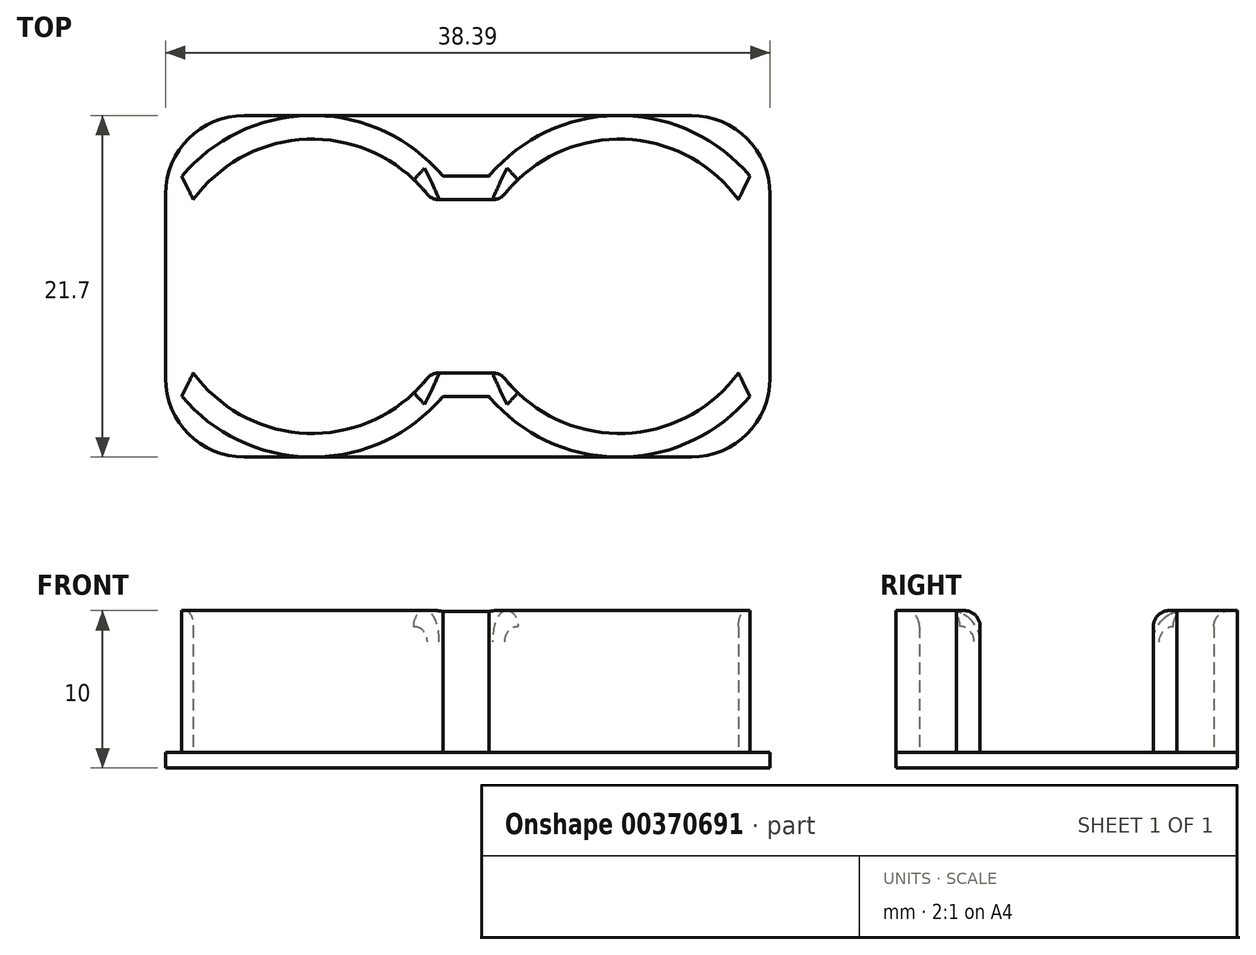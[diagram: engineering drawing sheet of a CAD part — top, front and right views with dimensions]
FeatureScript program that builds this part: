
annotation { "Feature Type Name" : "Feature", "Feature Type Description" : "" }
export const myFeature = defineFeature(function(context is Context, id is Id, definition is map)
    precondition{}
    {
        {
            var Q0;
            Q0=qCreatedBy(makeId("Top.planeOp"),FACE);
            var sketch = newSketch(context, id + "F0", { "sketchPlane" : qUnion([Q0])});
            skArc(sketch, "E0.1.0.0", {"start": v(11.94, -5.5) * mm, "mid": v(19.5, -9.35) * mm, "end": v(27.06, -5.5) * mm});
            skArc(sketch, "E0.2.0.0", {"start": v(31.44, -5.5) * mm, "mid": v(39, -9.35) * mm, "end": v(46.56, -5.5) * mm});
            skLineSegment(sketch, "E0.direction1", {"start": v(0, 0) * mm, "end": v(19.5, 0) * mm, "construction": true});
            skLineSegment(sketch, "E1.trimOffspring", {"start": v(27.06, 5.5) * mm, "end": v(31.44, 5.5) * mm});
            skLineSegment(sketch, "E2.MirrorCS", {"start": v(27.06, -5.5) * mm, "end": v(31.44, -5.5) * mm});
            skArc(sketch, "E3.trimOffspring", {"start": v(27.06, 5.5) * mm, "mid": v(19.5, 9.35) * mm, "end": v(11.94, 5.5) * mm});
            skArc(sketch, "E4.trimOffspring", {"start": v(46.56, 5.5) * mm, "mid": v(39, 9.35) * mm, "end": v(31.44, 5.5) * mm});
            skArc(sketch, "E5.3", {"start": v(47.29, 7) * mm, "mid": v(39, 10.85) * mm, "end": v(30.71, 7) * mm});
            skArc(sketch, "E5.7", {"start": v(30.71, -7) * mm, "mid": v(39, -10.85) * mm, "end": v(47.29, -7) * mm});
            skLineSegment(sketch, "E6.1.0.0", {"start": v(27.79, 7) * mm, "end": v(30.71, 7) * mm});
            skLineSegment(sketch, "E7.MirrorCS", {"start": v(27.79, -7) * mm, "end": v(30.71, -7) * mm});
            skArc(sketch, "E8.trimOffspring", {"start": v(27.79, 7) * mm, "mid": v(19.5, 10.85) * mm, "end": v(11.21, 7) * mm});
            skArc(sketch, "E9.trimOffspring", {"start": v(11.21, -7) * mm, "mid": v(19.5, -10.85) * mm, "end": v(27.79, -7) * mm});
            skLineSegment(sketch, "E10", {"start": v(11.94, 5.5) * mm, "end": v(11.21, 7) * mm});
            skLineSegment(sketch, "E11", {"start": v(46.56, 5.5) * mm, "end": v(47.29, 7) * mm});
            skLineSegment(sketch, "E12", {"start": v(47.29, -7) * mm, "end": v(46.56, -5.5) * mm});
            skLineSegment(sketch, "E13", {"start": v(11.21, -7) * mm, "end": v(11.94, -5.5) * mm});
            skSolve(sketch);
        }
        {
            var Q0;
            Q0=qCreatedBy(makeId("Top.planeOp"),FACE);
            var sketch = newSketch(context, id + "F1", { "sketchPlane" : qUnion([Q0])});
            skArc(sketch, "E14", {"start": v(7.52, 5.55) * mm, "mid": v(-9.35, 0) * mm, "end": v(7.52, -5.55) * mm});
            skArc(sketch, "E15.2.0.0", {"start": v(29.28, -5.55) * mm, "mid": v(36.8, -9.35) * mm, "end": v(44.32, -5.55) * mm});
            skLineSegment(sketch, "E15.direction1", {"start": v(0, 0) * mm, "end": v(18.5, 0) * mm, "construction": true});
            skArc(sketch, "E16.0", {"start": v(8.15, 7.16) * mm, "mid": v(-10.85, 0) * mm, "end": v(8.15, -7.16) * mm});
            skArc(sketch, "E17.0", {"start": v(28.65, -7.16) * mm, "mid": v(36.8, -10.85) * mm, "end": v(44.95, -7.16) * mm});
            skLineSegment(sketch, "E18", {"start": v(8.15, 7.16) * mm, "end": v(10.25, 7.16) * mm});
            skLineSegment(sketch, "E19.1.0.0", {"start": v(26.55, 7.16) * mm, "end": v(28.65, 7.16) * mm});
            skLineSegment(sketch, "E19.direction1", {"start": v(8.15, 7.16) * mm, "end": v(10.25, 7.16) * mm, "construction": true});
            skLineSegment(sketch, "E20", {"start": v(9.2, 5.55) * mm, "end": v(7.52, 5.55) * mm});
            skLineSegment(sketch, "E21", {"start": v(7.52, 5.55) * mm, "end": v(10.88, 5.55) * mm});
            skLineSegment(sketch, "E22.MirrorCS", {"start": v(8.15, -7.16) * mm, "end": v(10.25, -7.16) * mm});
            skLineSegment(sketch, "E23.MirrorCS", {"start": v(7.52, -5.55) * mm, "end": v(10.88, -5.55) * mm});
            skLineSegment(sketch, "E24.MirrorCS", {"start": v(26.55, -7.16) * mm, "end": v(28.65, -7.16) * mm});
            skLineSegment(sketch, "E25.MirrorCS", {"start": v(25.68, -5.55) * mm, "end": v(29.28, -5.55) * mm});
            skArc(sketch, "E26.trimOffspring", {"start": v(10.25, -7.16) * mm, "mid": v(18.4, -10.93) * mm, "end": v(26.55, -7.16) * mm});
            skArc(sketch, "E27.trimOffspring", {"start": v(10.88, -5.55) * mm, "mid": v(18.28, -9.29) * mm, "end": v(25.68, -5.55) * mm});
            skArc(sketch, "E28.trimOffspring", {"start": v(26.55, 7.16) * mm, "mid": v(18.4, 10.93) * mm, "end": v(10.25, 7.16) * mm});
            skArc(sketch, "E29.trimOffspring", {"start": v(25.68, 5.55) * mm, "mid": v(18.28, 9.29) * mm, "end": v(10.88, 5.55) * mm});
            skLineSegment(sketch, "E30", {"start": v(25.68, 5.55) * mm, "end": v(29.28, 5.55) * mm});
            skArc(sketch, "E31", {"start": v(62.82, 5.55) * mm, "mid": v(55.3, 9.35) * mm, "end": v(47.78, 5.55) * mm});
            skArc(sketch, "E32.2.0.0", {"start": v(84.58, -5.55) * mm, "mid": v(101.45, 0) * mm, "end": v(84.58, 5.55) * mm});
            skLineSegment(sketch, "E32.direction1", {"start": v(55.3, 0) * mm, "end": v(73.8, 0) * mm, "construction": true});
            skArc(sketch, "E33.0", {"start": v(63.45, 7.16) * mm, "mid": v(55.3, 10.85) * mm, "end": v(47.15, 7.16) * mm});
            skArc(sketch, "E34.0", {"start": v(83.95, -7.16) * mm, "mid": v(102.95, 0) * mm, "end": v(83.95, 7.16) * mm});
            skLineSegment(sketch, "E35", {"start": v(63.45, 7.16) * mm, "end": v(65.55, 7.16) * mm});
            skLineSegment(sketch, "E36.1.0.0", {"start": v(81.85, 7.16) * mm, "end": v(83.95, 7.16) * mm});
            skLineSegment(sketch, "E36.direction1", {"start": v(63.45, 7.16) * mm, "end": v(65.55, 7.16) * mm, "construction": true});
            skLineSegment(sketch, "E37", {"start": v(64.5, 5.55) * mm, "end": v(62.82, 5.55) * mm});
            skLineSegment(sketch, "E38", {"start": v(62.82, 5.55) * mm, "end": v(66.18, 5.55) * mm});
            skLineSegment(sketch, "E39.MirrorCS", {"start": v(63.45, -7.16) * mm, "end": v(65.55, -7.16) * mm});
            skLineSegment(sketch, "E40.MirrorCS", {"start": v(62.82, -5.55) * mm, "end": v(66.18, -5.55) * mm});
            skLineSegment(sketch, "E41.MirrorCS", {"start": v(81.85, -7.16) * mm, "end": v(83.95, -7.16) * mm});
            skLineSegment(sketch, "E42.MirrorCS", {"start": v(80.98, -5.55) * mm, "end": v(84.58, -5.55) * mm});
            skArc(sketch, "E43.trimOffspring", {"start": v(65.55, -7.16) * mm, "mid": v(73.7, -10.93) * mm, "end": v(81.85, -7.16) * mm});
            skArc(sketch, "E44.trimOffspring", {"start": v(66.18, -5.55) * mm, "mid": v(73.58, -9.29) * mm, "end": v(80.98, -5.55) * mm});
            skArc(sketch, "E45.trimOffspring", {"start": v(81.85, 7.16) * mm, "mid": v(73.7, 10.93) * mm, "end": v(65.55, 7.16) * mm});
            skArc(sketch, "E46.trimOffspring", {"start": v(80.98, 5.55) * mm, "mid": v(73.58, 9.29) * mm, "end": v(66.18, 5.55) * mm});
            skLineSegment(sketch, "E47", {"start": v(80.98, 5.55) * mm, "end": v(84.58, 5.55) * mm});
            skLineSegment(sketch, "E48.0.3.0", {"start": v(63.35, 7.16) * mm, "end": v(65.45, 7.16) * mm});
            skLineSegment(sketch, "E49", {"start": v(44.95, 7.16) * mm, "end": v(47.15, 7.16) * mm});
            skLineSegment(sketch, "E50", {"start": v(44.95, -7.16) * mm, "end": v(47.15, -7.16) * mm});
            skLineSegment(sketch, "E51", {"start": v(44.32, -5.55) * mm, "end": v(47.78, -5.55) * mm});
            skLineSegment(sketch, "E52", {"start": v(44.32, 5.55) * mm, "end": v(47.78, 5.55) * mm});
            skPoint(sketch, "E52.startSnap0", {"position": v(27.48, 5.55) * mm});
            skArc(sketch, "E53.trimOffspring", {"start": v(44.95, 7.16) * mm, "mid": v(36.8, 10.85) * mm, "end": v(28.65, 7.16) * mm});
            skArc(sketch, "E54.trimOffspring", {"start": v(46.05, 5.67) * mm, "mid": v(46.01, 5.61) * mm, "end": v(45.98, 5.55) * mm});
            skArc(sketch, "E55.trimOffspring", {"start": v(46.12, 5.55) * mm, "mid": v(46.09, 5.61) * mm, "end": v(46.05, 5.67) * mm});
            skArc(sketch, "E56.trimOffspring", {"start": v(47.78, -5.55) * mm, "mid": v(55.3, -9.35) * mm, "end": v(62.82, -5.55) * mm});
            skArc(sketch, "E57.trimOffspring", {"start": v(44.32, 5.55) * mm, "mid": v(36.8, 9.35) * mm, "end": v(29.28, 5.55) * mm});
            skArc(sketch, "E58.trimOffspring", {"start": v(45.98, -5.55) * mm, "mid": v(46.01, -5.61) * mm, "end": v(46.05, -5.67) * mm});
            skArc(sketch, "E59.trimOffspring", {"start": v(46.05, -5.67) * mm, "mid": v(46.09, -5.61) * mm, "end": v(46.12, -5.55) * mm});
            skArc(sketch, "E60.trimOffspring", {"start": v(47.15, -7.16) * mm, "mid": v(55.3, -10.85) * mm, "end": v(63.45, -7.16) * mm});
            skSolve(sketch);
        }
        {
            var Q0;
            Q0=makeQuery(id+"F0.imprint","IMPRINT",FACE,{"disambiguationData":[TD([[makeQuery(id+"F0.imprint","IMPRINT",EDGE,{"derivedFrom":sQuery(id+"F0.wireOp",EDGE,"E1.trimOffspring")}),1.0]])]});
            var Q1;
            Q1=makeQuery(id+"F0.imprint","IMPRINT",FACE,{"disambiguationData":[TD([[makeQuery(id+"F0.imprint","IMPRINT",EDGE,{"derivedFrom":sQuery(id+"F0.wireOp",EDGE,"E0.1.0.0")}),-1.0]])]});
            extrude(context, id + "F2", {"entities" : qUnion([Q0, Q1]), "depth" : 10 * mm, "offsetDistance" : 25 * mm});
        }
        {
            var Q0;
            Q0=qCreatedBy(makeId("Top.planeOp"),FACE);
            var sketch = newSketch(context, id + "F3", { "sketchPlane" : qUnion([Q0])});
            skLineSegment(sketch, "E61.bottom", {"start": v(10.17, -10.85) * mm, "end": v(48.56, -10.85) * mm});
            skLineSegment(sketch, "E61.top", {"start": v(10.17, 10.85) * mm, "end": v(48.56, 10.85) * mm});
            skLineSegment(sketch, "E61.left", {"start": v(10.17, -10.85) * mm, "end": v(10.17, 10.85) * mm});
            skLineSegment(sketch, "E61.right", {"start": v(48.56, -10.85) * mm, "end": v(48.56, 10.85) * mm});
            skPoint(sketch, "E61.middle", {"position": v(29.37, 0) * mm});
            skCircle(sketch, "E62", {"center": v(39.18, 0) * mm, "radius": 9.3 * mm, "construction": true});
            skCircle(sketch, "E63", {"center": v(19.56, 0) * mm, "radius": 9.27 * mm, "construction": true});
            skSolve(sketch);
        }
        {
            var Q0;
            Q0=makeQuery(id+"F3.imprint","IMPRINT",FACE,{"disambiguationData":[TD([[makeQuery(id+"F3.imprint","IMPRINT",EDGE,{"derivedFrom":sQuery(id+"F3.wireOp",EDGE,"E61.bottom")}),1.0]])]});
            extrude(context, id + "F4", {"entities" : qUnion([Q0]), "operationType" : NewBodyOperationType.ADD, "depth" : 1 * mm, "offsetDistance" : 25 * mm});
        }
        {
            var Q0;
            Q0=makeQuery(id+"F4.opExtrude","SWEPT_EDGE",EDGE,{"disambiguationData":[OSD([sQuery(id+"F3.wireOp",EDGE,"E61.bottom"),sQuery(id+"F3.wireOp",EDGE,"E61.left")])]});
            var Q1;
            Q1=makeQuery(id+"F4.opExtrude","SWEPT_EDGE",EDGE,{"disambiguationData":[OSD([sQuery(id+"F3.wireOp",EDGE,"E61.bottom"),sQuery(id+"F3.wireOp",EDGE,"E61.right")])]});
            var Q2;
            Q2=makeQuery(id+"F4.opExtrude","SWEPT_EDGE",EDGE,{"disambiguationData":[OSD([sQuery(id+"F3.wireOp",EDGE,"E61.top"),sQuery(id+"F3.wireOp",EDGE,"E61.left")])]});
            var Q3;
            Q3=makeQuery(id+"F4.opExtrude","SWEPT_EDGE",EDGE,{"disambiguationData":[OSD([sQuery(id+"F3.wireOp",EDGE,"E61.top"),sQuery(id+"F3.wireOp",EDGE,"E61.right")])]});
            fillet(context, id + "F5", {"entities" : qUnion([Q0, Q1, Q2, Q3]), "radius" : 5 * mm, "tangentPropagation" : true, "allowEdgeOverflow" : false});
        }
        {
            var Q0;
            Q0=qCreatedBy(makeId("Right.planeOp"),FACE);
            var sketch = newSketch(context, id + "F6", { "sketchPlane" : qUnion([Q0])});
            skLineSegment(sketch, "E64.bottom", {"start": v(-5.5, 1) * mm, "end": v(5.5, 1) * mm});
            skLineSegment(sketch, "E64.top", {"start": v(-5.5, 51) * mm, "end": v(5.5, 51) * mm});
            skLineSegment(sketch, "E64.left", {"start": v(-5.5, 1) * mm, "end": v(-5.5, 51) * mm});
            skLineSegment(sketch, "E64.right", {"start": v(5.5, 1) * mm, "end": v(5.5, 51) * mm});
            skPoint(sketch, "E64.middle", {"position": v(0, 26) * mm});
            skSolve(sketch);
        }
        {
            var Q0;
            Q0=makeQuery(id+"F2.opExtrude","CAP_EDGE",EDGE,{"disambiguationData":[OSD([sQuery(id+"F1.wireOp",EDGE,"E21")])],"isStart":false});
            var Q1;
            Q1=makeQuery(id+"F2.opExtrude","CAP_EDGE",EDGE,{"disambiguationData":[OSD([sQuery(id+"F1.wireOp",EDGE,"E30")])],"isStart":false});
            var Q2;
            {var subQ0=sQuery(id+"F1.wireOp",EDGE,"E52");Q2=makeQuery(id+"F2.opExtrude","CAP_EDGE",EDGE,{"disambiguationData":[OSD([subQ0]),TDD([makeQuery(id+"F1.imprint","IMPRINT",EDGE,{"disambiguationData":[TD([[makeQuery(id+"F1.imprint","INTERSECT",VERTEX,{"derivedFrom":[subQ0,sQuery(id+"F1.wireOp",EDGE,"E57.trimOffspring")]}),-1.0]])],"derivedFrom":subQ0})])],"isStart":false});}
            var Q3;
            Q3=makeQuery(id+"F2.opExtrude","CAP_EDGE",EDGE,{"disambiguationData":[OSD([sQuery(id+"F1.wireOp",EDGE,"E38")])],"isStart":false});
            var Q4;
            Q4=makeQuery(id+"F2.opExtrude","CAP_EDGE",EDGE,{"disambiguationData":[OSD([sQuery(id+"F1.wireOp",EDGE,"E47")])],"isStart":false});
            var Q5;
            Q5=makeQuery(id+"F2.opExtrude","CAP_EDGE",EDGE,{"disambiguationData":[OSD([sQuery(id+"F1.wireOp",EDGE,"E23.MirrorCS")])],"isStart":false});
            var Q6;
            Q6=makeQuery(id+"F2.opExtrude","CAP_EDGE",EDGE,{"disambiguationData":[OSD([sQuery(id+"F1.wireOp",EDGE,"E25.MirrorCS")])],"isStart":false});
            var Q7;
            {var subQ0=sQuery(id+"F1.wireOp",EDGE,"E51");Q7=makeQuery(id+"F2.opExtrude","CAP_EDGE",EDGE,{"disambiguationData":[OSD([subQ0]),TDD([makeQuery(id+"F1.imprint","IMPRINT",EDGE,{"disambiguationData":[TD([[makeQuery(id+"F1.imprint","INTERSECT",VERTEX,{"derivedFrom":[sQuery(id+"F1.wireOp",EDGE,"E15.2.0.0"),subQ0]}),-1.0]])],"derivedFrom":subQ0})])],"isStart":false});}
            var Q8;
            Q8=makeQuery(id+"F2.opExtrude","CAP_EDGE",EDGE,{"disambiguationData":[OSD([sQuery(id+"F1.wireOp",EDGE,"E40.MirrorCS")])],"isStart":false});
            var Q9;
            Q9=makeQuery(id+"F2.opExtrude","CAP_EDGE",EDGE,{"disambiguationData":[OSD([sQuery(id+"F1.wireOp",EDGE,"E42.MirrorCS")])],"isStart":false});
            var Q10;
            Q10=makeQuery(id+"FvLSEFZZQq34Obx_1.boolean.opBoolean","INTERSECT",EDGE,{"derivedFrom":[makeQuery(id+"F2.opExtrude","CAP_FACE",FACE,{"disambiguationData":[OSD([sQuery(id+"F1.wireOp",EDGE,"E14"),sQuery(id+"F1.wireOp",EDGE,"E15.2.0.0"),sQuery(id+"F1.wireOp",EDGE,"E16.0"),sQuery(id+"F1.wireOp",EDGE,"E17.0"),sQuery(id+"F1.wireOp",EDGE,"E18"),sQuery(id+"F1.wireOp",EDGE,"E19.1.0.0"),sQuery(id+"F1.wireOp",EDGE,"E21"),sQuery(id+"F1.wireOp",EDGE,"E22.MirrorCS"),sQuery(id+"F1.wireOp",EDGE,"E23.MirrorCS"),sQuery(id+"F1.wireOp",EDGE,"E24.MirrorCS"),sQuery(id+"F1.wireOp",EDGE,"E25.MirrorCS"),sQuery(id+"F1.wireOp",EDGE,"E26.trimOffspring"),sQuery(id+"F1.wireOp",EDGE,"E27.trimOffspring"),sQuery(id+"F1.wireOp",EDGE,"E28.trimOffspring"),sQuery(id+"F1.wireOp",EDGE,"E29.trimOffspring"),sQuery(id+"F1.wireOp",EDGE,"E30"),sQuery(id+"F1.wireOp",EDGE,"E31"),sQuery(id+"F1.wireOp",EDGE,"E32.2.0.0"),sQuery(id+"F1.wireOp",EDGE,"E33.0"),sQuery(id+"F1.wireOp",EDGE,"E34.0"),sQuery(id+"F1.wireOp",EDGE,"E35"),sQuery(id+"F1.wireOp",EDGE,"E36.1.0.0"),sQuery(id+"F1.wireOp",EDGE,"E38"),sQuery(id+"F1.wireOp",EDGE,"E39.MirrorCS"),sQuery(id+"F1.wireOp",EDGE,"E40.MirrorCS"),sQuery(id+"F1.wireOp",EDGE,"E41.MirrorCS"),sQuery(id+"F1.wireOp",EDGE,"E42.MirrorCS"),sQuery(id+"F1.wireOp",EDGE,"E43.trimOffspring"),sQuery(id+"F1.wireOp",EDGE,"E44.trimOffspring"),sQuery(id+"F1.wireOp",EDGE,"E45.trimOffspring"),sQuery(id+"F1.wireOp",EDGE,"E46.trimOffspring"),sQuery(id+"F1.wireOp",EDGE,"E47"),sQuery(id+"F1.wireOp",EDGE,"E48.0.3.0"),sQuery(id+"F1.wireOp",EDGE,"E49"),sQuery(id+"F1.wireOp",EDGE,"E50"),sQuery(id+"F1.wireOp",EDGE,"E51"),sQuery(id+"F1.wireOp",EDGE,"E52"),sQuery(id+"F1.wireOp",EDGE,"E53.trimOffspring"),sQuery(id+"F1.wireOp",EDGE,"E54.trimOffspring"),sQuery(id+"F1.wireOp",EDGE,"E55.trimOffspring"),sQuery(id+"F1.wireOp",EDGE,"E56.trimOffspring"),sQuery(id+"F1.wireOp",EDGE,"E57.trimOffspring"),sQuery(id+"F1.wireOp",EDGE,"E58.trimOffspring"),sQuery(id+"F1.wireOp",EDGE,"E59.trimOffspring"),sQuery(id+"F1.wireOp",EDGE,"E60.trimOffspring")])],"isStart":false}),makeQuery(id+"FvLSEFZZQq34Obx_1.opExtrude","SWEPT_FACE",FACE,{"disambiguationData":[OSD([sQuery(id+"F6.wireOp",EDGE,"E64.left")])]})]});
            var Q11;
            Q11=makeQuery(id+"FvLSEFZZQq34Obx_1.boolean.opBoolean","INTERSECT",EDGE,{"derivedFrom":[makeQuery(id+"F2.opExtrude","CAP_FACE",FACE,{"disambiguationData":[OSD([sQuery(id+"F1.wireOp",EDGE,"E14"),sQuery(id+"F1.wireOp",EDGE,"E15.2.0.0"),sQuery(id+"F1.wireOp",EDGE,"E16.0"),sQuery(id+"F1.wireOp",EDGE,"E17.0"),sQuery(id+"F1.wireOp",EDGE,"E18"),sQuery(id+"F1.wireOp",EDGE,"E19.1.0.0"),sQuery(id+"F1.wireOp",EDGE,"E21"),sQuery(id+"F1.wireOp",EDGE,"E22.MirrorCS"),sQuery(id+"F1.wireOp",EDGE,"E23.MirrorCS"),sQuery(id+"F1.wireOp",EDGE,"E24.MirrorCS"),sQuery(id+"F1.wireOp",EDGE,"E25.MirrorCS"),sQuery(id+"F1.wireOp",EDGE,"E26.trimOffspring"),sQuery(id+"F1.wireOp",EDGE,"E27.trimOffspring"),sQuery(id+"F1.wireOp",EDGE,"E28.trimOffspring"),sQuery(id+"F1.wireOp",EDGE,"E29.trimOffspring"),sQuery(id+"F1.wireOp",EDGE,"E30"),sQuery(id+"F1.wireOp",EDGE,"E31"),sQuery(id+"F1.wireOp",EDGE,"E32.2.0.0"),sQuery(id+"F1.wireOp",EDGE,"E33.0"),sQuery(id+"F1.wireOp",EDGE,"E34.0"),sQuery(id+"F1.wireOp",EDGE,"E35"),sQuery(id+"F1.wireOp",EDGE,"E36.1.0.0"),sQuery(id+"F1.wireOp",EDGE,"E38"),sQuery(id+"F1.wireOp",EDGE,"E39.MirrorCS"),sQuery(id+"F1.wireOp",EDGE,"E40.MirrorCS"),sQuery(id+"F1.wireOp",EDGE,"E41.MirrorCS"),sQuery(id+"F1.wireOp",EDGE,"E42.MirrorCS"),sQuery(id+"F1.wireOp",EDGE,"E43.trimOffspring"),sQuery(id+"F1.wireOp",EDGE,"E44.trimOffspring"),sQuery(id+"F1.wireOp",EDGE,"E45.trimOffspring"),sQuery(id+"F1.wireOp",EDGE,"E46.trimOffspring"),sQuery(id+"F1.wireOp",EDGE,"E47"),sQuery(id+"F1.wireOp",EDGE,"E48.0.3.0"),sQuery(id+"F1.wireOp",EDGE,"E49"),sQuery(id+"F1.wireOp",EDGE,"E50"),sQuery(id+"F1.wireOp",EDGE,"E51"),sQuery(id+"F1.wireOp",EDGE,"E52"),sQuery(id+"F1.wireOp",EDGE,"E53.trimOffspring"),sQuery(id+"F1.wireOp",EDGE,"E54.trimOffspring"),sQuery(id+"F1.wireOp",EDGE,"E55.trimOffspring"),sQuery(id+"F1.wireOp",EDGE,"E56.trimOffspring"),sQuery(id+"F1.wireOp",EDGE,"E57.trimOffspring"),sQuery(id+"F1.wireOp",EDGE,"E58.trimOffspring"),sQuery(id+"F1.wireOp",EDGE,"E59.trimOffspring"),sQuery(id+"F1.wireOp",EDGE,"E60.trimOffspring")])],"isStart":false}),makeQuery(id+"FvLSEFZZQq34Obx_1.opExtrude","SWEPT_FACE",FACE,{"disambiguationData":[OSD([sQuery(id+"F6.wireOp",EDGE,"E64.right")])]})]});
            var Q12;
            Q12=makeQuery(id+"F2.opExtrude","CAP_EDGE",EDGE,{"disambiguationData":[OSD([sQuery(id+"F0.wireOp",EDGE,"Owk9uptJ-Jh1L-xAo9-dw1z-BDvCM43XCUK6")])],"isStart":false});
            var Q13;
            Q13=makeQuery(id+"F2.opExtrude","CAP_EDGE",EDGE,{"disambiguationData":[OSD([sQuery(id+"F0.wireOp",EDGE,"E1.trimOffspring")])],"isStart":false});
            var Q14;
            Q14=makeQuery(id+"F2.opExtrude","CAP_EDGE",EDGE,{"disambiguationData":[OSD([sQuery(id+"F0.wireOp",EDGE,"6d046082-f231-4d7b-a296-89ed1bad6cdd.trimOffspring")])],"isStart":false});
            var Q15;
            Q15=makeQuery(id+"F2.opExtrude","CAP_EDGE",EDGE,{"disambiguationData":[OSD([sQuery(id+"F0.wireOp",EDGE,"612d0de8-0294-4495-ac26-fdf52f0d9c6e.trimOffspring")])],"isStart":false});
            var Q16;
            Q16=makeQuery(id+"F2.opExtrude","CAP_EDGE",EDGE,{"disambiguationData":[OSD([sQuery(id+"F0.wireOp",EDGE,"a985cf25-736e-43ae-8161-f681ec351d08.trimOffspring")])],"isStart":false});
            var Q17;
            Q17=makeQuery(id+"F2.opExtrude","CAP_EDGE",EDGE,{"disambiguationData":[OSD([sQuery(id+"F0.wireOp",EDGE,"0fe0c3fc-aee3-45be-8472-b9a6150ec706.trimOffspring")])],"isStart":false});
            var Q18;
            Q18=makeQuery(id+"F2.opExtrude","CAP_EDGE",EDGE,{"disambiguationData":[OSD([sQuery(id+"F0.wireOp",EDGE,"90a56129-1c10-42f6-bc15-1a9e8192e6bf0.MirrorCS")])],"isStart":false});
            var Q19;
            Q19=makeQuery(id+"F2.opExtrude","CAP_EDGE",EDGE,{"disambiguationData":[OSD([sQuery(id+"F0.wireOp",EDGE,"d214c793-d903-466d-81b3-8aefb3d0225e0.MirrorCS")])],"isStart":false});
            var Q20;
            Q20=makeQuery(id+"F2.opExtrude","CAP_EDGE",EDGE,{"disambiguationData":[OSD([sQuery(id+"F0.wireOp",EDGE,"0405b32a-29e1-4415-a3fd-83d8df7a473a0.MirrorCS")])],"isStart":false});
            var Q21;
            Q21=makeQuery(id+"F2.opExtrude","CAP_EDGE",EDGE,{"disambiguationData":[OSD([sQuery(id+"F0.wireOp",EDGE,"00a0a44e-3ef1-4cd6-8e2f-0b575c23ec7e0.MirrorCS")])],"isStart":false});
            var Q22;
            Q22=makeQuery(id+"F2.opExtrude","CAP_EDGE",EDGE,{"disambiguationData":[OSD([sQuery(id+"F0.wireOp",EDGE,"E2.MirrorCS")])],"isStart":false});
            var Q23;
            Q23=makeQuery(id+"F2.opExtrude","CAP_EDGE",EDGE,{"disambiguationData":[OSD([sQuery(id+"F0.wireOp",EDGE,"f19aa527-6b91-4a43-9dd2-eb869203c6bc0.MirrorCS")])],"isStart":false});
            fillet(context, id + "F7", {"entities" : qUnion([Q0, Q1, Q2, Q3, Q4, Q5, Q6, Q7, Q8, Q9, Q10, Q11, Q12, Q13, Q14, Q15, Q16, Q17, Q18, Q19, Q20, Q21, Q22, Q23]), "radius" : 2 * mm, "tangentPropagation" : true, "allowEdgeOverflow" : false});
        }
        {
            var Q0;
            Q0=makeQuery(id+"F2.opExtrude","CAP_EDGE",EDGE,{"disambiguationData":[OSD([sQuery(id+"F0.wireOp",EDGE,"5d4U6IWx-X6N6-tDBP-mZHH-Fz7w98qtp8wK")])],"isStart":false});
            var Q1;
            Q1=makeQuery(id+"F2.opExtrude","CAP_EDGE",EDGE,{"disambiguationData":[OSD([sQuery(id+"F0.wireOp",EDGE,"E3.trimOffspring")])],"isStart":false});
            var Q2;
            Q2=makeQuery(id+"F2.opExtrude","CAP_EDGE",EDGE,{"disambiguationData":[OSD([sQuery(id+"F0.wireOp",EDGE,"E4.trimOffspring")])],"isStart":false});
            var Q3;
            Q3=makeQuery(id+"F2.opExtrude","CAP_EDGE",EDGE,{"disambiguationData":[OSD([sQuery(id+"F0.wireOp",EDGE,"c5e36073-e61a-4c7b-a4d3-11c86a808830.trimOffspring")])],"isStart":false});
            var Q4;
            Q4=makeQuery(id+"F2.opExtrude","CAP_EDGE",EDGE,{"disambiguationData":[OSD([sQuery(id+"F0.wireOp",EDGE,"be0627fa-58c3-4c0f-9c73-5aa1584e8e68.trimOffspring")])],"isStart":false});
            var Q5;
            Q5=makeQuery(id+"F2.opExtrude","CAP_EDGE",EDGE,{"disambiguationData":[OSD([sQuery(id+"F0.wireOp",EDGE,"6ef7e5e5-10de-4270-b966-e9febad0215a.trimOffspring")])],"isStart":false});
            var Q6;
            Q6=makeQuery(id+"F2.opExtrude","CAP_EDGE",EDGE,{"disambiguationData":[OSD([sQuery(id+"F0.wireOp",EDGE,"296380e1-93f9-4f33-b404-91d8a0943d40.0.6.0")])],"isStart":false});
            var Q7;
            Q7=makeQuery(id+"F2.opExtrude","CAP_EDGE",EDGE,{"disambiguationData":[OSD([sQuery(id+"F0.wireOp",EDGE,"296380e1-93f9-4f33-b404-91d8a0943d40.0.5.0")])],"isStart":false});
            var Q8;
            Q8=makeQuery(id+"F2.opExtrude","CAP_EDGE",EDGE,{"disambiguationData":[OSD([sQuery(id+"F0.wireOp",EDGE,"296380e1-93f9-4f33-b404-91d8a0943d40.0.4.0")])],"isStart":false});
            var Q9;
            Q9=makeQuery(id+"F2.opExtrude","CAP_EDGE",EDGE,{"disambiguationData":[OSD([sQuery(id+"F0.wireOp",EDGE,"296380e1-93f9-4f33-b404-91d8a0943d40.0.3.0")])],"isStart":false});
            var Q10;
            Q10=makeQuery(id+"F2.opExtrude","CAP_EDGE",EDGE,{"disambiguationData":[OSD([sQuery(id+"F0.wireOp",EDGE,"E0.2.0.0")])],"isStart":false});
            var Q11;
            Q11=makeQuery(id+"F2.opExtrude","CAP_EDGE",EDGE,{"disambiguationData":[OSD([sQuery(id+"F0.wireOp",EDGE,"E0.1.0.0")])],"isStart":false});
            fillet(context, id + "F8", {"entities" : qUnion([Q0, Q1, Q2, Q3, Q4, Q5, Q6, Q7, Q8, Q9, Q10, Q11]), "radius" : 1 * mm, "tangentPropagation" : true, "allowEdgeOverflow" : false});
        }
    });
